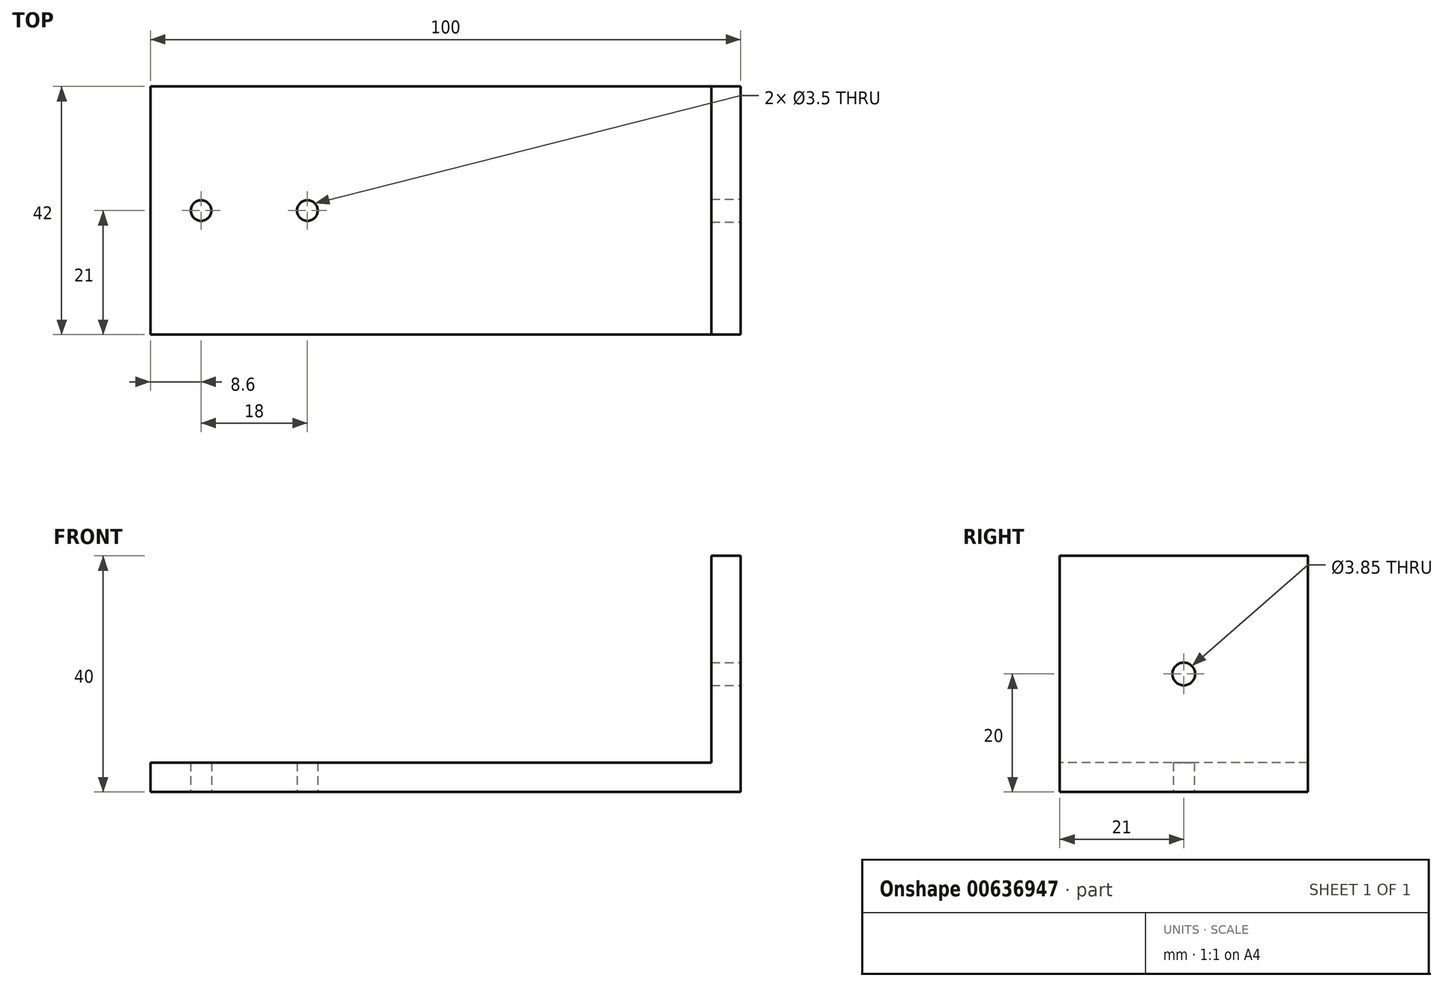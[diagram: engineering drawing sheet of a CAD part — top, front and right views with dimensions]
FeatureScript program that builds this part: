
annotation { "Feature Type Name" : "Feature", "Feature Type Description" : "" }
export const myFeature = defineFeature(function(context is Context, id is Id, definition is map)
    precondition{}
    {
        {
            var Q0;
            Q0=qCreatedBy(makeId("Top.planeOp"),FACE);
            var sketch = newSketch(context, id + "F0", { "sketchPlane" : qUnion([Q0])});
            skLineSegment(sketch, "E0.bottom", {"start": v(-47.5, 21) * mm, "end": v(47.5, 21) * mm});
            skLineSegment(sketch, "E0.top", {"start": v(-47.5, -21) * mm, "end": v(47.5, -21) * mm});
            skLineSegment(sketch, "E0.left", {"start": v(-47.5, 21) * mm, "end": v(-47.5, -21) * mm});
            skPoint(sketch, "E0.middle", {"position": v(0, 0) * mm});
            skPoint(sketch, "E1.centerSnap0", {"position": v(-47.5, 0) * mm});
            skLineSegment(sketch, "E2", {"start": v(-47.5, 0) * mm, "end": v(-38.9, 0) * mm});
            skLineSegment(sketch, "E3", {"start": v(-38.9, 0) * mm, "end": v(-20.9, 0) * mm});
            skCircle(sketch, "E4", {"center": v(-38.9, 0) * mm, "radius": 1.75 * mm});
            skCircle(sketch, "E5", {"center": v(-20.9, 0) * mm, "radius": 1.75 * mm});
            skLineSegment(sketch, "E6", {"start": v(47.5, 21) * mm, "end": v(47.5, -21) * mm});
            skLineSegment(sketch, "E7.bottom", {"start": v(47.5, 21) * mm, "end": v(52.5, 21) * mm});
            skLineSegment(sketch, "E7.top", {"start": v(47.5, -21) * mm, "end": v(52.5, -21) * mm});
            skLineSegment(sketch, "E7.right", {"start": v(52.5, 21) * mm, "end": v(52.5, -21) * mm});
            skSolve(sketch);
        }
        {
            var Q0;
            Q0=makeQuery(id+"F0.imprint","IMPRINT",FACE,{"disambiguationData":[TD([[makeQuery(id+"F0.imprint","IMPRINT",EDGE,{"derivedFrom":sQuery(id+"F0.wireOp",EDGE,"E7.bottom")}),-1.0]])]});
            extrude(context, id + "F1", {"entities" : qUnion([Q0]), "depth" : 40 * mm, "offsetDistance" : 25 * mm});
        }
        {
            var Q0;
            {var subQ3=sQuery(id+"F0.wireOp",EDGE,"E0.bottom");Q0=makeQuery(id+"F0.imprint","IMPRINT",FACE,{"disambiguationData":[TD([[makeQuery(id+"F0.imprint","IMPRINT",EDGE,{"derivedFrom":subQ3}),-1.0]])]});}
            extrude(context, id + "F2", {"entities" : qUnion([Q0]), "operationType" : NewBodyOperationType.ADD, "depth" : 5 * mm, "offsetDistance" : 25 * mm});
        }
        {
            var Q0;
            Q0=makeQuery(id+"F1.opExtrude","SWEPT_FACE",FACE,{"disambiguationData":[OSD([sQuery(id+"F0.wireOp",EDGE,"E7.right")])]});
            var sketch = newSketch(context, id + "F3", { "sketchPlane" : qUnion([Q0])});
            skLineSegment(sketch, "E8", {"start": v(0, 0) * mm, "end": v(0, 20) * mm});
            skCircle(sketch, "E9", {"center": v(0, 20) * mm, "radius": 1.92 * mm});
            skSolve(sketch);
        }
        {
            var Q0;
            Q0=makeQuery(id+"F3.imprint","IMPRINT",FACE,{"disambiguationData":[TD([[makeQuery(id+"F3.imprint","IMPRINT",EDGE,{"derivedFrom":sQuery(id+"F3.wireOp",EDGE,"E9")}),1.0]])]});
            extrude(context, id + "F4", {"entities" : qUnion([Q0]), "operationType" : NewBodyOperationType.REMOVE, "oppositeDirection" : true, "depth" : 5 * mm, "offsetDistance" : 25 * mm});
        }
    });
